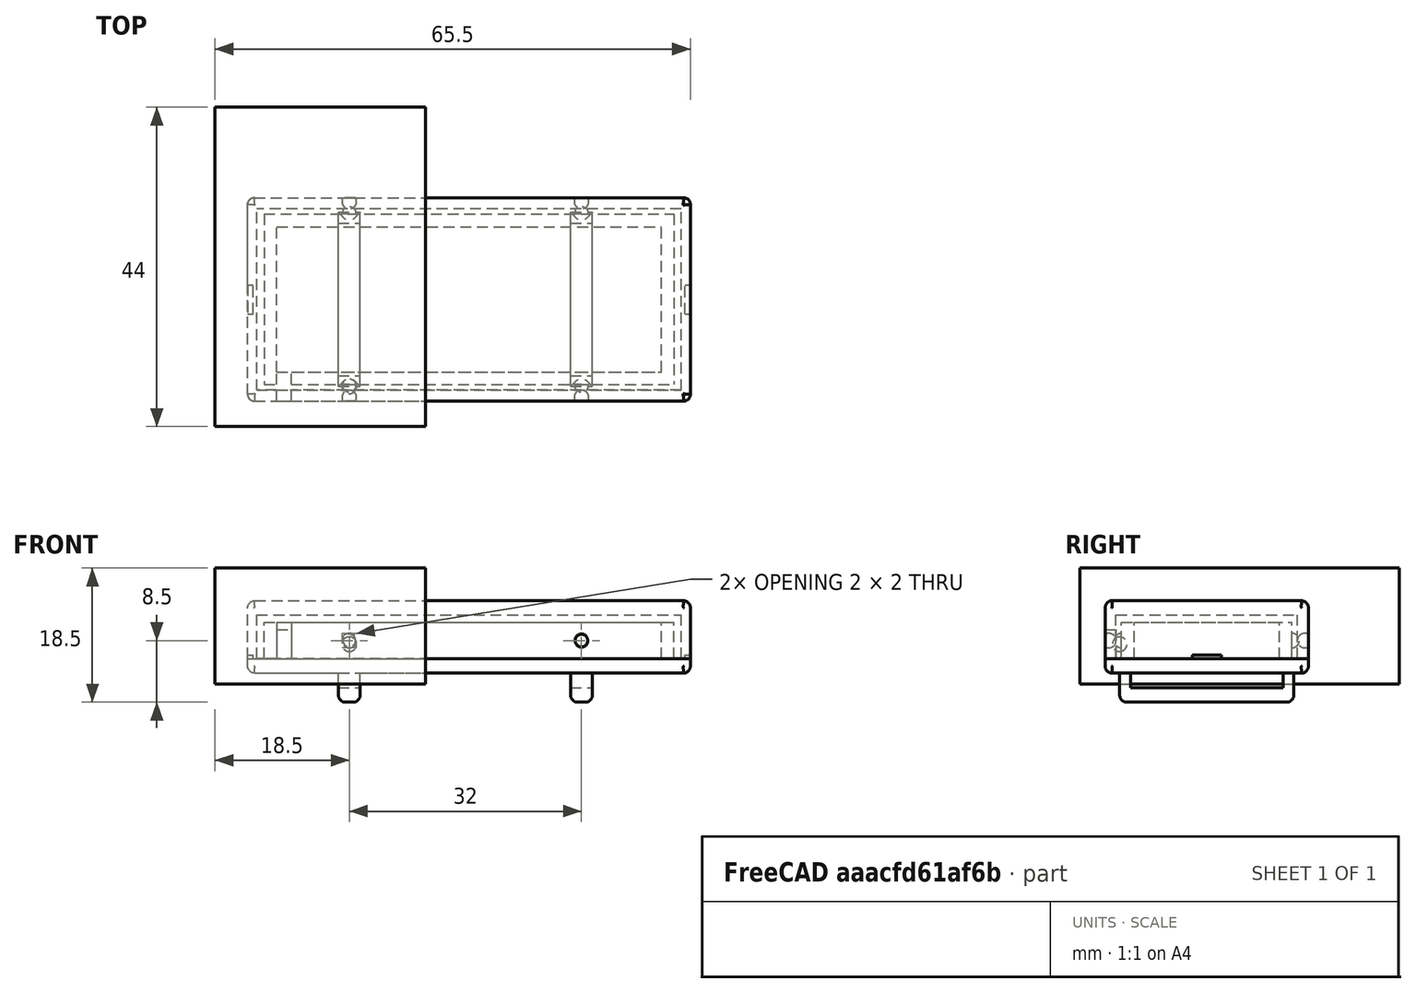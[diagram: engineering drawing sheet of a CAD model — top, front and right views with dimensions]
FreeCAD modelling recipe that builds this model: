
FCSTD DOCUMENT  (FreeCAD 0.21R33771 (Git))
Label: Batteriecasing rev 4
License: All rights reserved
LicenseURL: https://en.wikipedia.org/wiki/All_rights_reserved
objects: Part::Box×13, App::Link×12, Part::Cut×11, Part::Fillet×5, Part::Sphere×2, Part::MultiFuse×2, App::LinkGroup×1
note: 33 computed .brp shape members not serialized (recipe doc carries the construction recipe); baked Part::Feature solids carry a one-line shape summary decoded from their .brp

FEATURE [Part::Box] Box  label="Batterie"
  AttacherType = Attacher::AttachEngine3D
  Height = 5
  Length = 53
  Width = 20
FEATURE [Part::Box] Box001  label="Base"
  AttacherType = Attacher::AttachEngine3D
  Height = 8
  Length = 58.5
  Placement = pos=(-2.75,-2.5,-2) rot=(0,0,1;0rad)
  Width = 25
FEATURE [Part::Box] Box002  label="Würfel001"
  AttacherType = Attacher::AttachEngine3D
  Height = 8
  Length = 61
  Placement = pos=(-4,-4,0) rot=(0,0,1;0rad)
  Width = 28
FEATURE [Part::Cut] Cut001
  Base = -> Box002
  Tool = -> Box001
FEATURE [Part::Sphere] Sphere  label="Noppel1"
  Angle1 = -90
  Angle2 = 90
  Angle3 = 360
  AttacherType = Attacher::AttachEngine3D
  Placement = pos=(10,-2,2) rot=(0,0,1;0rad)
  Radius = 1
FEATURE [App::Link] Link002  label="Noppel2"
  LinkPlacement = pos=(42,-2,1.5) rot=(0,0,1;0rad)
  LinkedObject = -> Sphere
  Placement = pos=(42,-2,1.5) rot=(0,0,1;0rad)
FEATURE [App::Link] Link003  label="Noppel003"
  LinkPlacement = pos=(42,-3.5,2.5) rot=(0,0,1;0rad)
  LinkedObject = -> Link002
  Placement = pos=(42,-3.5,2.5) rot=(0,0,1;0rad)
FEATURE [Part::Cut] Cut002
  Base = -> Cut001
  Tool = -> Link003
FEATURE [App::Link] Link004  label="Noppel004"
  LinkPlacement = pos=(10,-3.5,2.5) rot=(0,0,1;0rad)
  LinkedObject = -> Sphere
  Placement = pos=(10,-3.5,2.5) rot=(0,0,1;0rad)
FEATURE [Part::Cut] Cut003
  Base = -> Cut002
  Tool = -> Link004
FEATURE [App::Link] Link005  label="Noppel3"
  LinkPlacement = pos=(10,22,1.5) rot=(0,0,1;0rad)
  LinkedObject = -> Sphere
  Placement = pos=(10,22,1.5) rot=(0,0,1;0rad)
FEATURE [App::Link] Link006  label="Noppel4"
  LinkPlacement = pos=(42,22,1.5) rot=(0,0,1;0rad)
  LinkedObject = -> Sphere
  Placement = pos=(42,22,1.5) rot=(0,0,1;0rad)
FEATURE [App::Link] Link007  label="Noppel005"
  LinkPlacement = pos=(10,23.5,2.5) rot=(0,0,1;0rad)
  LinkedObject = -> Link005
  Placement = pos=(10,23.5,2.5) rot=(0,0,1;0rad)
FEATURE [Part::Cut] Cut004
  Base = -> Cut003
  Tool = -> Link007
FEATURE [App::Link] Link008  label="Noppel006"
  LinkPlacement = pos=(42,23.5,2.5) rot=(0,0,1;0rad)
  LinkedObject = -> Link006
  Placement = pos=(42,23.5,2.5) rot=(0,0,1;0rad)
FEATURE [Part::Cut] Cut005  label="Cut007"
  Base = -> Cut004
  Tool = -> Link008
FEATURE [Part::Box] Box004  label="Würfel003"
  AttacherType = Attacher::AttachEngine3D
  Height = 6
  Length = 2
  Placement = pos=(0,-4.25,-2) rot=(0,0,1;0rad)
  Width = 2
FEATURE [Part::Cut] Cut007  label="Cut008"
  Base = -> Cut005
  Tool = -> Box004
FEATURE [Part::Box] Box007  label="Batterie002"
  AttacherType = Attacher::AttachEngine3D
  Height = 5
  Length = 53
  Width = 20
FEATURE [Part::Box] Box008  label="Base001"
  AttacherType = Attacher::AttachEngine3D
  Height = 7
  Length = 56.5
  Placement = pos=(-1.75,-1.75,-2) rot=(0,0,1;0rad)
  Width = 23.5
FEATURE [Part::Box] Box009  label="Würfel006"
  AttacherType = Attacher::AttachEngine3D
  Height = 5
  Length = 2
  Placement = pos=(0,-2,0) rot=(0,0,1;0rad)
  Width = 2
FEATURE [Part::Box] Box010  label="Würfel007"
  AttacherType = Attacher::AttachEngine3D
  Height = 4
  Length = 3
  Placement = pos=(8.5,-2,-6) rot=(0,0,1;0rad)
  Width = 24
FEATURE [Part::Box] Box011  label="Würfel008"
  AttacherType = Attacher::AttachEngine3D
  Height = 2
  Length = 3
  Placement = pos=(8.5,-0.5,-4) rot=(0,0,1;0rad)
  Width = 21
FEATURE [Part::Cut] Cut011  label="Cut012"
  Base = -> Box010
  Tool = -> Box011
FEATURE [Part::Fillet] Fillet002  label="Fillet003"
  Base = -> Cut011
  Edges = 4 edges r=1: [Edge7,Edge20,Edge22,Edge23]
FEATURE [App::Link] Link010  label="Batterie003"
  LinkedObject = -> Box007
FEATURE [Part::Cut] Cut009  label="Cut010"
  Base = -> Box008
  Tool = -> Link010
FEATURE [App::Link] Link011  label="Noppel007"
  LinkPlacement = pos=(42,-1.75,2.5) rot=(0,0,1;0rad)
  LinkedObject = -> Sphere001
  Placement = pos=(42,-1.75,2.5) rot=(0,0,1;0rad)
FEATURE [App::Link] Link012  label="Noppel008"
  LinkPlacement = pos=(10,21.75,2.5) rot=(0,0,1;0rad)
  LinkedObject = -> Sphere001
  Placement = pos=(10,21.75,2.5) rot=(0,0,1;0rad)
FEATURE [App::Link] Link013  label="Noppel009"
  LinkPlacement = pos=(42,21.75,2.5) rot=(0,0,1;0rad)
  LinkedObject = -> Sphere001
  Placement = pos=(42,21.75,2.5) rot=(0,0,1;0rad)
FEATURE [App::Link] Link014  label="Fillet004"
  LinkPlacement = pos=(32,-3.8147e-06,0) rot=(0,0,1;0rad)
  LinkedObject = -> Fillet002
  Placement = pos=(32,-3.8147e-06,0) rot=(0,0,1;0rad)
FEATURE [Part::Sphere] Sphere001  label="Noppel010"
  Angle1 = -90
  Angle2 = 90
  Angle3 = 360
  AttacherType = Attacher::AttachEngine3D
  Placement = pos=(10,-1.75,2.5) rot=(0,0,1;0rad)
  Radius = 1
FEATURE [Part::MultiFuse] Fusion002  label="Cut013"
  Shapes = -> [Cut009,Sphere001,Link011,Link012,Link013]
FEATURE [Part::Cut] Cut010  label="Cut011"
  Base = -> Fusion002
  Tool = -> Box009
FEATURE [App::LinkGroup] LinkGroup  label="Other stuff"
  ElementList = -> [Link006,Sphere,Link002,Link005,Box007]
  LinkMode = 0
FEATURE [Part::Box] Box012  label="Würfel"
  AttacherType = Attacher::AttachEngine3D
  Height = 2
  Length = 61
  Placement = pos=(-4,-4,-2) rot=(0,0,1;0rad)
  Width = 28
FEATURE [Part::MultiFuse] Fusion003
  Shapes = -> [Cut010,Fillet002,Link014,Box012]
FEATURE [Part::Fillet] Fillet
  Base = -> Cut007
  Edges = 4 edges r=1: [Edge2,Edge11,Edge14,Edge15]
FEATURE [Part::Fillet] Fillet003  label="Fillet005"
  Base = -> Fusion003
  Edges = 4 edges r=1: [Edge4,Edge5,Edge16,Edge18]
FEATURE [Part::Fillet] Fillet004  label="Fillet006"
  Base = -> Fillet
  Edges = 4 edges r=0.9: [Edge1,Edge3,Edge5,Edge26]
FEATURE [Part::Fillet] Fillet005  label="Fillet007"
  Base = -> Fillet003
  Edges = 4 edges r=0.9: [Edge1,Edge3,Edge5,Edge19]
FEATURE [Part::Box] Box013  label="Schnit"
  AttacherType = Attacher::AttachEngine3D
  Height = 16
  Length = 29
  Placement = pos=(-8.5,-7.5,-3.5) rot=(0,0,1;0rad)
  Width = 44
FEATURE [Part::Box] Box014  label="Würfel009"
  AttacherType = Attacher::AttachEngine3D
  Height = 0.5
  Length = 2
  Placement = pos=(-5.25,8,0) rot=(0,0,1;0rad)
  Width = 4
FEATURE [Part::Cut] Cut
  Base = -> Fillet004
  Tool = -> Box014
FEATURE [Part::Box] Box015  label="Würfel010"
  AttacherType = Attacher::AttachEngine3D
  Height = 0.5
  Length = 2
  Placement = pos=(56.25,8,0) rot=(0,0,1;0rad)
  Width = 4
FEATURE [Part::Cut] Cut012  label="Cut014"
  Base = -> Cut
  Tool = -> Box015
